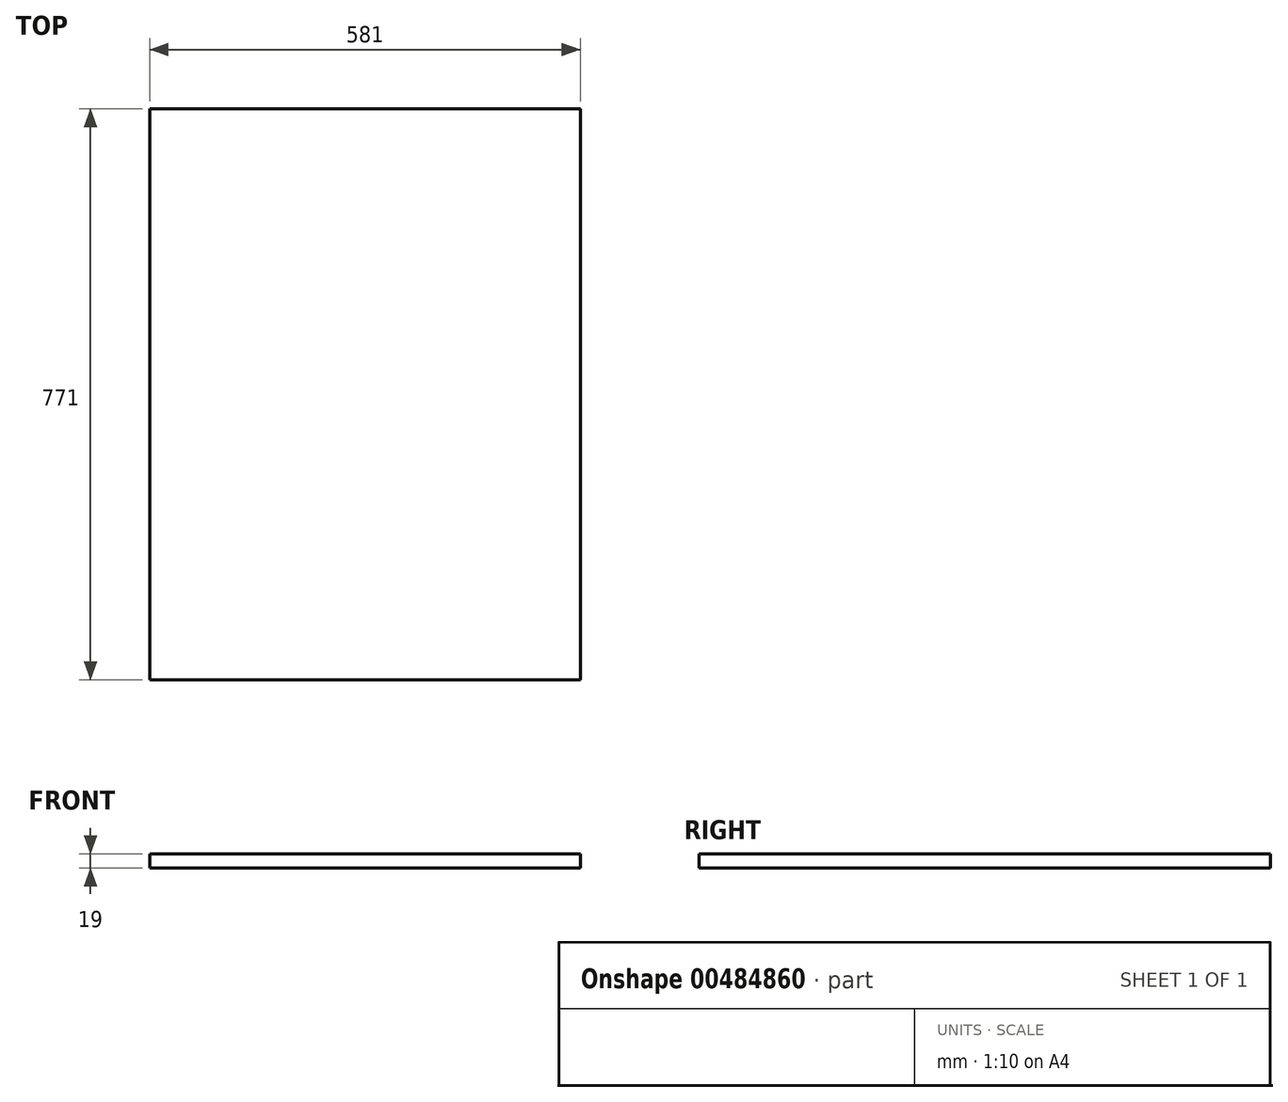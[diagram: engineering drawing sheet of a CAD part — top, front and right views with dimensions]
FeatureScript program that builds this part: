
annotation { "Feature Type Name" : "Feature", "Feature Type Description" : "" }
export const myFeature = defineFeature(function(context is Context, id is Id, definition is map)
    precondition{}
    {
        {
            var Q0;
            Q0=qCreatedBy(makeId("Top.planeOp"),FACE);
            var sketch = newSketch(context, id + "F0", { "sketchPlane" : qUnion([Q0])});
            skLineSegment(sketch, "E0.bottom", {"start": v(-265.55, 649.04) * mm, "end": v(315.45, 649.04) * mm});
            skLineSegment(sketch, "E0.top", {"start": v(-265.55, -121.96) * mm, "end": v(315.45, -121.96) * mm});
            skLineSegment(sketch, "E0.left", {"start": v(-265.55, 649.04) * mm, "end": v(-265.55, -121.96) * mm});
            skLineSegment(sketch, "E0.right", {"start": v(315.45, 649.04) * mm, "end": v(315.45, -121.96) * mm});
            skSolve(sketch);
        }
        {
            var Q0;
            Q0=makeQuery(id+"F0.imprint","IMPRINT",FACE,{"disambiguationData":[TD([[makeQuery(id+"F0.imprint","IMPRINT",EDGE,{"derivedFrom":sQuery(id+"F0.wireOp",EDGE,"E0.bottom")}),-1.0]])]});
            extrude(context, id + "F1", {"entities" : qUnion([Q0]), "depth" : 19 * mm});
        }
    });
